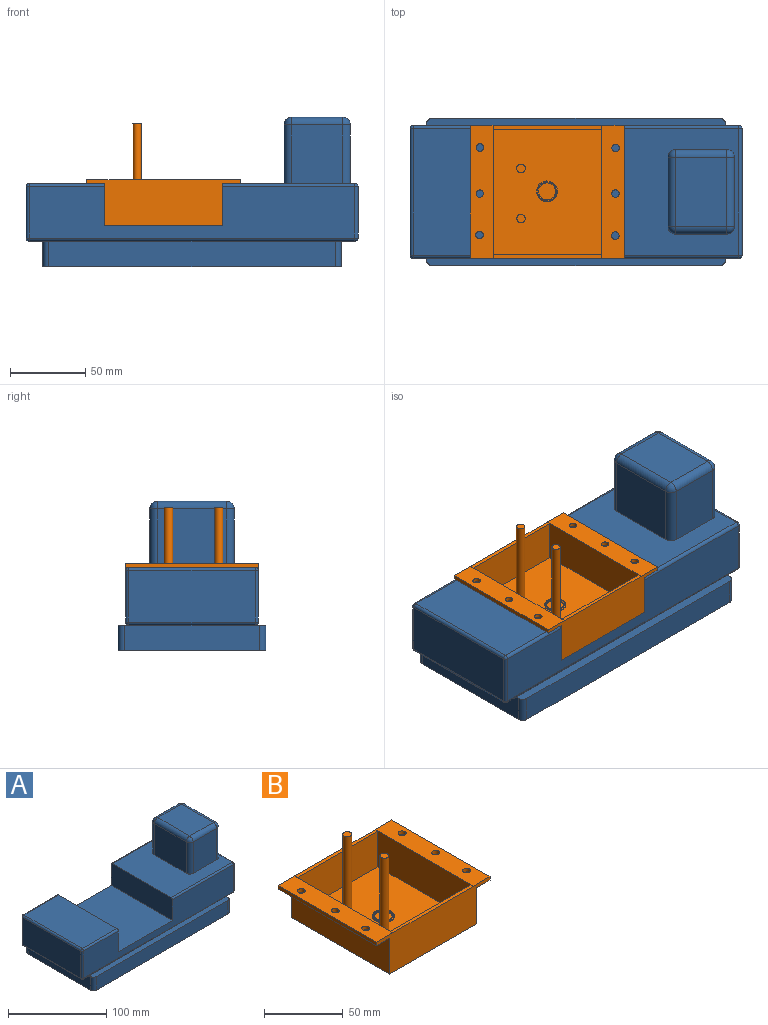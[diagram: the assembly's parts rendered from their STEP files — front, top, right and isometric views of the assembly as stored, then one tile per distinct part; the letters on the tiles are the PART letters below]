
ASSEMBLY  parts=2 mates=1
PART A: 61 faces, bbox 220x98x99 mm
  f0: plane 198x7mm, normal (0,0,1), area 1379.1mm2, adj f2,f3,f4,f7,f8,f37
  f1: plane 198x7mm, normal (0,0,1), area 1379.1mm2, adj f2,f4,f5,f9,f10,f29
  f2: plane 90x17mm, normal (-1,0,0), area 1530mm2, adj f0,f1,f6,f7,f10,f11
  f3: plane 190x17mm, normal (0,-1,0), area 3230mm2, adj f0,f6,f7,f8
  f4: plane 90x17mm, normal (1,0,0), area 1530mm2, adj f0,f1,f6,f8,f9,f18
  f5: plane 190x17mm, normal (0,1,0), area 3230mm2, adj f1,f6,f9,f10
  f6: plane 198x98mm, normal (0,0,-1), area 19390.3mm2, adj f2,f3,f4,f5,f7,f8,f9,f10
  f7: cylinder r=4mm len=17mm, axis (0,0,-1), area 106.8mm2, adj f0,f2,f3,f6
  f8: cylinder r=4mm len=17mm, axis (0,0,1), area 106.8mm2, adj f0,f3,f4,f6
  f9: cylinder r=4mm len=17mm, axis (0,0,-1), area 106.8mm2, adj f1,f4,f5,f6
  f10: cylinder r=4mm len=17mm, axis (0,0,1), area 106.8mm2, adj f1,f2,f5,f6
  f11: plane 84x9mm, normal (0,0,-1), area 756mm2, adj f2,f29,f30,f37
  f12: plane 88x84mm, normal (0,0,1), area 4949.5mm2, adj f19,f34,f40,f43,f44,f45,f46,f47
  f13: plane 216x34mm, normal (0,-1,0), area 5316mm2, adj f19,f20,f21,f26,f31,f37,f41,f43
  f14: plane 216x34mm, normal (0,1,0), area 5316mm2, adj f19,f20,f21,f22,f24,f29,f34,f35
  f15: plane 84x34mm, normal (-1,0,0), area 2856mm2, adj f24,f25,f30,f31
  f16: plane 84x34mm, normal (1,0,0), area 2856mm2, adj f35,f36,f40,f41
  f17: plane 84x50mm, normal (0,0,1), area 4200mm2, adj f20,f22,f25,f26
  f18: plane 84x9mm, normal (0,0,-1), area 756mm2, adj f4,f29,f36,f37
  f19: plane 88x28mm, normal (-1,0,0), area 2462.3mm2, adj f12,f13,f14,f21,f34,f43
  f20: plane 88x28mm, normal (1,0,0), area 2462.3mm2, adj f13,f14,f17,f21,f22,f26
  f21: plane 88x78mm, normal (0,0,1), area 6864mm2, adj f13,f14,f19,f20
  f22: cylinder r=2mm len=50mm, axis (1,0,0), area 157.1mm2, adj f14,f17,f20,f23
  f23: sphere r=2mm, area 6.3mm2, adj f22,f24,f25
  f24: cylinder r=2mm len=34mm, axis (0,0,1), area 106.8mm2, adj f14,f15,f23,f27
  f25: cylinder r=2mm len=84mm, axis (0,1,0), area 263.9mm2, adj f15,f17,f23,f28
  f26: cylinder r=2mm len=50mm, axis (-1,0,0), area 157.1mm2, adj f13,f17,f20,f28
  f27: sphere r=2mm, area 6.3mm2, adj f24,f29,f30
  f28: sphere r=2mm, area 6.3mm2, adj f25,f26,f31
  f29: cylinder r=2mm len=216mm, axis (-1,0,0), area 678.6mm2, adj f1,f11,f14,f18,f27,f32
  f30: cylinder r=2mm len=84mm, axis (0,-1,0), area 263.9mm2, adj f11,f15,f27,f33
  f31: cylinder r=2mm len=34mm, axis (0,0,-1), area 106.8mm2, adj f13,f15,f28,f33
  f32: sphere r=2mm, area 6.3mm2, adj f29,f35,f36
  f33: sphere r=2mm, area 6.3mm2, adj f30,f31,f37
  f34: cylinder r=2mm len=88mm, axis (1,0,0), area 276.5mm2, adj f12,f14,f19,f38
  f35: cylinder r=2mm len=34mm, axis (0,0,-1), area 106.8mm2, adj f14,f16,f32,f38
  f36: cylinder r=2mm len=84mm, axis (0,1,0), area 263.9mm2, adj f16,f18,f32,f39
  f37: cylinder r=2mm len=216mm, axis (1,0,0), area 678.6mm2, adj f0,f11,f13,f18,f33,f39
  f38: sphere r=2mm, area 6.3mm2, adj f34,f35,f40
  f39: sphere r=2mm, area 6.3mm2, adj f36,f37,f41
  f40: cylinder r=2mm len=84mm, axis (0,-1,0), area 263.9mm2, adj f12,f16,f38,f42
  f41: cylinder r=2mm len=34mm, axis (0,0,1), area 106.8mm2, adj f13,f16,f39,f42
  f42: sphere r=2mm, area 6.3mm2, adj f40,f41,f43
  f43: cylinder r=2mm len=88mm, axis (-1,0,0), area 276.5mm2, adj f12,f13,f19,f42
  f44: plane 39x34mm, normal (0,-1,0), area 1326mm2, adj f12,f51,f57,f60
  f45: plane 46x39mm, normal (1,0,0), area 1794mm2, adj f12,f54,f58,f60
  f46: plane 39x34mm, normal (0,1,0), area 1326mm2, adj f12,f49,f53,f54
  f47: plane 46x39mm, normal (-1,0,0), area 1794mm2, adj f12,f49,f51,f52
  f48: plane 46x34mm, normal (0,0,1), area 1564mm2, adj f52,f53,f57,f58
  f49: cylinder r=5mm len=39mm, axis (0,0,-1), area 306.3mm2, adj f12,f46,f47,f50
  f50: sphere r=5mm, area 39.3mm2, adj f49,f52,f53
  f51: cylinder r=5mm len=39mm, axis (0,0,1), area 306.3mm2, adj f12,f44,f47,f55
  f52: cylinder r=5mm len=46mm, axis (0,1,0), area 361.3mm2, adj f47,f48,f50,f55
  f53: cylinder r=5mm len=34mm, axis (1,0,0), area 267mm2, adj f46,f48,f50,f56
  f54: cylinder r=5mm len=39mm, axis (0,0,1), area 306.3mm2, adj f12,f45,f46,f56
  f55: sphere r=5mm, area 39.3mm2, adj f51,f52,f57
  f56: sphere r=5mm, area 39.3mm2, adj f53,f54,f58
  f57: cylinder r=5mm len=34mm, axis (-1,0,0), area 267mm2, adj f44,f48,f55,f59
  f58: cylinder r=5mm len=46mm, axis (0,-1,0), area 361.3mm2, adj f45,f48,f56,f59
  f59: sphere r=5mm, area 39.3mm2, adj f57,f58,f60
  f60: cylinder r=5mm len=39mm, axis (0,0,-1), area 306.3mm2, adj f12,f44,f45,f59
PART B: 34 faces, bbox 102x88x68 mm
  f0: plane 88x27.75mm, normal (-1,0,0), area 2307.8mm2, adj f1,f11,f12,f13,f20,f21,f22,f23
  f1: plane 83.14x72mm, normal (0,0,1), area 5786.1mm2, adj f0,f2,f20,f22,f24,f30,f32
  f2: plane 88x27.75mm, normal (1,0,0), area 2307.8mm2, adj f1,f3,f12,f13,f20,f21,f22,f23
  f3: plane 88x15mm, normal (0,0,1), area 1262.2mm2, adj f2,f4,f12,f13,f17,f18,f19
  f4: plane 88x2.75mm, normal (-1,0,0), area 241.9mm2, adj f3,f5,f12,f13
  f5: plane 88x12mm, normal (0,0,-1), area 998.1mm2, adj f4,f6,f12,f13,f17,f18,f19
  f6: plane 88x28mm, normal (-1,0,0), area 2464mm2, adj f5,f7,f12,f13
  f7: plane 88x78mm, normal (0,0,-1), area 6864mm2, adj f6,f8,f12,f13
  f8: plane 88x28mm, normal (1,0,0), area 2464mm2, adj f7,f9,f12,f13
  f9: plane 88x12mm, normal (0,0,-1), area 997.4mm2, adj f8,f10,f12,f13,f14,f15,f16
  f10: plane 88x2.75mm, normal (1,0,0), area 241.9mm2, adj f9,f11,f12,f13
  f11: plane 88x15mm, normal (0,0,1), area 1261.5mm2, adj f0,f10,f12,f13,f14,f15,f16
  f12: plane 102x30.75mm, normal (0,-1,0), area 2453.6mm2, adj f0,f2,f3,f4,f5,f6,f7,f8
  f13: plane 102x30.75mm, normal (0,1,0), area 2453.6mm2, adj f0,f2,f3,f4,f5,f6,f7,f8
  f14: cylinder r=2.47mm len=4.95mm, axis (0,0,1), area 42.7mm2, adj f9,f11
  f15: cylinder r=2.5mm len=5mm, axis (0,0,1), area 43.2mm2, adj f9,f11
  f16: cylinder r=2.5mm len=5mm, axis (0,0,1), area 43.2mm2, adj f9,f11
  f17: cylinder r=2.5mm len=5mm, axis (0,0,1), area 43.2mm2, adj f3,f5
  f18: cylinder r=2.43mm len=4.86mm, axis (0,0,1), area 41.9mm2, adj f3,f5
  f19: cylinder r=2.5mm len=5mm, axis (0,0,1), area 43.2mm2, adj f3,f5
  f20: plane 72x27.6mm, normal (0,-1,0), area 1987.1mm2, adj f0,f1,f2,f21
  f21: plane 72x2.49mm, normal (0,0,1), area 179.3mm2, adj f0,f2,f13,f20
  f22: plane 72x27.6mm, normal (0,1,0), area 1987.1mm2, adj f0,f1,f2,f23
  f23: plane 72x2.37mm, normal (0,0,1), area 170.4mm2, adj f0,f2,f12,f22
  f24: cylinder r=6.92mm len=13.84mm, axis (0,0,-1), area 21.7mm2, adj f1,f29
  f25: plane 12.84x12.84mm, normal (0,0,1), area 11.6mm2, adj f28,f29
  f26: cylinder r=5.63mm len=11.25mm, axis (0,0,1), area 17.7mm2, adj f27,f28
  f27: plane 11.25x11.25mm, normal (0,0,1), area 99.5mm2, adj f26
  f28: torus R=6.13mm, axis (0,0,1), area 28.7mm2, adj f25,f26
  f29: torus R=6.42mm, axis (0,0,1), area 33.3mm2, adj f24,f25
  f30: cylinder r=2.83mm len=65mm, axis (0,0,-1), area 1157.6mm2, adj f1,f31
  f31: plane 5.67x5.67mm, normal (0,0,1), area 25.2mm2, adj f30
  f32: cylinder r=2.79mm len=65mm, axis (0,0,-1), area 1137.8mm2, adj f1,f33
  f33: plane 5.57x5.57mm, normal (0,0,1), area 24.4mm2, adj f32
PLACE A t=(26.33,19.57,6.81)mm
PLACE B t=(20.31,14.76,43.44)mm
MATE fastened B.f7 <-> A.f21  axis (0,0,1) through (17.34,14.76,33.81)mm
